# Revit family: COPL COLUMN LIGHT
name_source: partatom
category: Lighting Fixtures
units: mm (PartAtom-declared; Revit-internal decimal feet)

## family parameters
Always vertical = Yes
Cut with Voids When Loaded = No
Light Source = Yes
Part Type = Normal
Room Calculation Point = No
Round Connector Dimension = Use Diameter
Shared = No
Work Plane-Based = No

## types (2) — shared parameters
Apparent Load = 38 VA
Base Width = 11 "
CRI = 70
Color Filter = 16777215
Description = The COPL column led light has elegant, slim and column design. It brings architectural style to any 
area or site, impacting pedestrian-scale for improved comfort and security.  High quality aluminum 
body, polycarbonate shade, moulded silicone gasket and stainless steel screws. This pole light is 
an excellent choice for walkways, entrances, promenades, plazas, courtyards, driveways, bridges,
and landscaped areas.
Dimming Lamp Color Temperature Shift = <None>
Emit from Line Length = 24 "
Fixture Diameter = 7.87 "
Fixture Radius = 3.94 "
IP Rating = 65
Manufacturer = Above All Lighting
Photometric Web File = COPL-30401-BK.IES
Tilt Angle = 90.00°
Type Comments = COPL COLUMN LIGHT
URL = https://www.abovealllighting.com
Voltage = 120 V
Voltage Comments = 120-277
WATTS = 30 W
zero-valued in all types: Default Elevation

## per-type parameters (varying)
| type | BOLT | Fixture Height | Pole Height |
| COPL-2.7 PLOE-BK | <By Category> | 137.77 " | 106.3 " |
| COPL-4.5 POLE-BK | Steel | 208.64 " | 177.17 " |

note: column(s) folded — value = type name in every type: Model

## geometry (parser evidence)
native form markers: Sweep x2
no freeform markers — native parametric forms only
